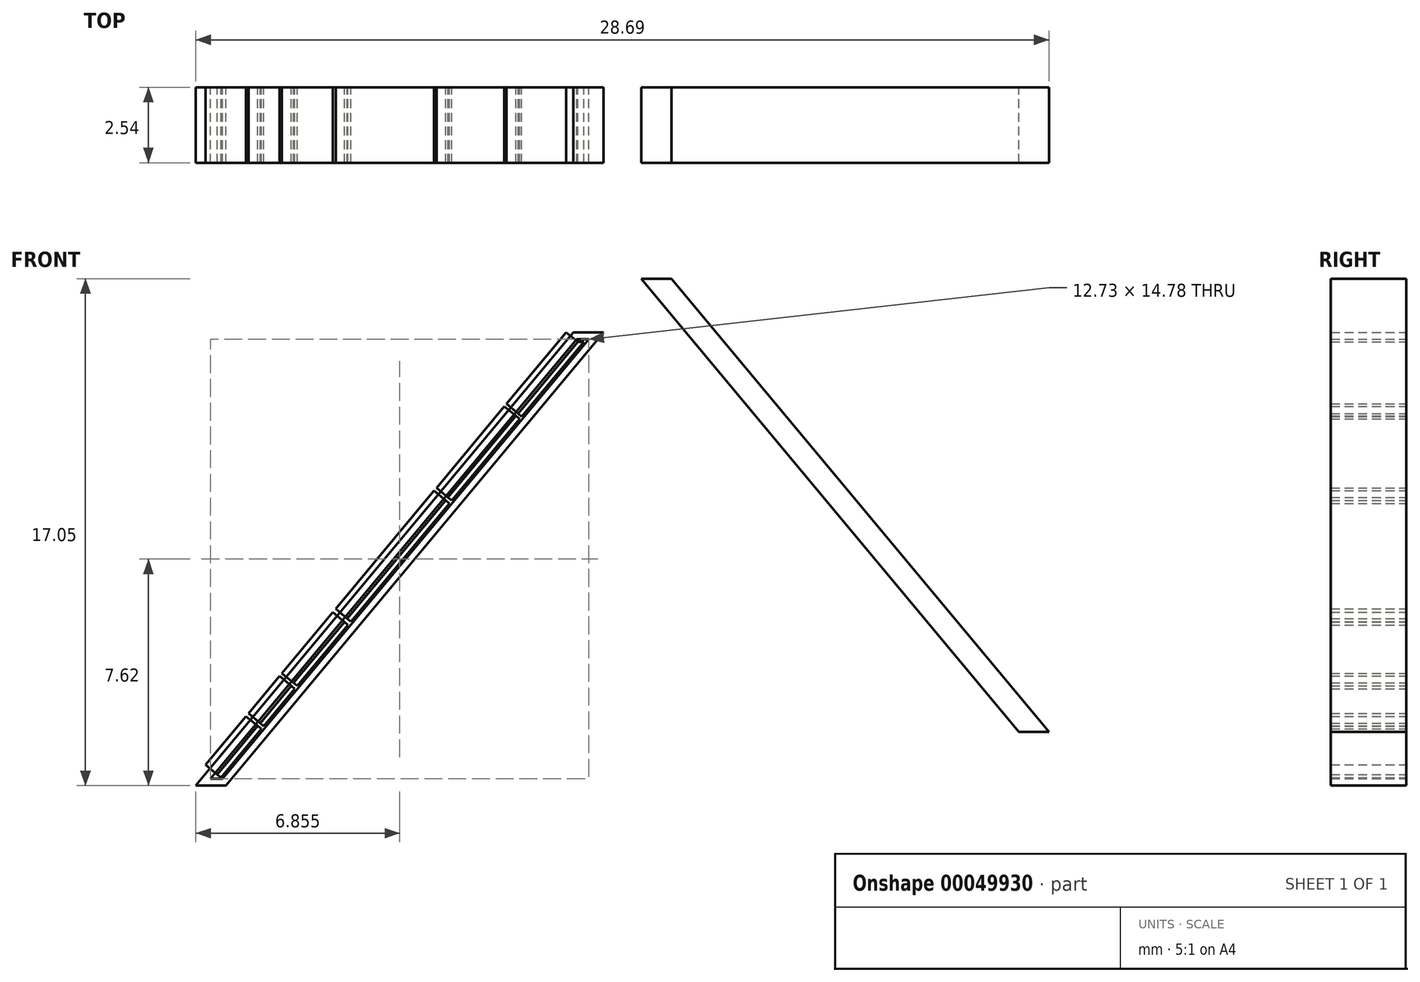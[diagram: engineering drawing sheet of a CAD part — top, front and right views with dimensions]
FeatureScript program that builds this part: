
annotation { "Feature Type Name" : "Feature", "Feature Type Description" : "" }
export const myFeature = defineFeature(function(context is Context, id is Id, definition is map)
    precondition{}
    {
        {
            var Q0;
            Q0=qCreatedBy(makeId("Front.planeOp"),FACE);
            var sketch = newSketch(context, id + "F0", { "sketchPlane" : qUnion([Q0])});
            skLineSegment(sketch, "E0", {"start": v(36.54, 21.91) * mm, "end": v(23.84, 6.67) * mm});
            skLineSegment(sketch, "E1", {"start": v(23.84, 6.67) * mm, "end": v(24.85, 6.67) * mm, "construction": true});
            skLineSegment(sketch, "E2", {"start": v(36.54, 21.91) * mm, "end": v(37.55, 21.91) * mm});
            skLineSegment(sketch, "E3", {"start": v(37.55, 21.91) * mm, "end": v(24.85, 6.67) * mm});
            skLineSegment(sketch, "E4", {"start": v(23.84, 6.67) * mm, "end": v(24.14, 6.67) * mm});
            skLineSegment(sketch, "E5", {"start": v(24.85, 6.67) * mm, "end": v(24.55, 6.67) * mm});
            skLineSegment(sketch, "E6", {"start": v(24.14, 6.67) * mm, "end": v(36.84, 21.91) * mm});
            skLineSegment(sketch, "E7", {"start": v(24.55, 6.67) * mm, "end": v(37.25, 21.91) * mm});
            skPoint(sketch, "E7.endSnap0", {"position": v(37.04, 21.91) * mm});
            skLineSegment(sketch, "E8", {"start": v(36.84, 21.91) * mm, "end": v(36.84, 21.68) * mm});
            skLineSegment(sketch, "E9", {"start": v(36.84, 21.68) * mm, "end": v(36.65, 21.68) * mm});
            skLineSegment(sketch, "E10", {"start": v(36.65, 21.68) * mm, "end": v(37.06, 21.68) * mm});
            skLineSegment(sketch, "E11", {"start": v(24.34, 6.67) * mm, "end": v(24.34, 6.9) * mm});
            skLineSegment(sketch, "E12", {"start": v(24.34, 6.9) * mm, "end": v(24.74, 6.9) * mm});
            skLineSegment(sketch, "E13", {"start": v(24.74, 6.9) * mm, "end": v(24.33, 6.9) * mm});
            skLineSegment(sketch, "E14", {"start": v(24.14, 6.67) * mm, "end": v(24.55, 6.67) * mm});
            skLineSegment(sketch, "E15", {"start": v(24.56, 6.9) * mm, "end": v(24.56, 7.04) * mm});
            skLineSegment(sketch, "E16", {"start": v(24.56, 7.04) * mm, "end": v(24.45, 7.04) * mm});
            skLineSegment(sketch, "E17", {"start": v(24.56, 7.04) * mm, "end": v(24.81, 7.35) * mm});
            skLineSegment(sketch, "E18", {"start": v(24.81, 7.35) * mm, "end": v(24.93, 7.25) * mm});
            skLineSegment(sketch, "E19", {"start": v(24.56, 7.04) * mm, "end": v(24.68, 6.94) * mm});
            skLineSegment(sketch, "E20", {"start": v(24.93, 7.25) * mm, "end": v(24.68, 6.94) * mm});
            skLineSegment(sketch, "E21", {"start": v(24.81, 7.35) * mm, "end": v(24.87, 7.42) * mm});
            skPoint(sketch, "E21.endSnap0", {"position": v(24.87, 7.3) * mm});
            skLineSegment(sketch, "E22", {"start": v(24.87, 7.42) * mm, "end": v(24.99, 7.32) * mm});
            skLineSegment(sketch, "E23", {"start": v(24.99, 7.32) * mm, "end": v(25.32, 7.72) * mm});
            skLineSegment(sketch, "E24", {"start": v(24.87, 7.42) * mm, "end": v(25.2, 7.82) * mm});
            skLineSegment(sketch, "E25", {"start": v(25.2, 7.82) * mm, "end": v(25.32, 7.72) * mm});
            skLineSegment(sketch, "E26", {"start": v(25.2, 7.82) * mm, "end": v(25.24, 7.86) * mm});
            skLineSegment(sketch, "E27", {"start": v(25.24, 7.86) * mm, "end": v(25.35, 7.77) * mm});
            skLineSegment(sketch, "E28", {"start": v(25.35, 7.77) * mm, "end": v(25.51, 7.96) * mm});
            skLineSegment(sketch, "E29", {"start": v(25.24, 7.86) * mm, "end": v(25.4, 8.05) * mm});
            skLineSegment(sketch, "E30", {"start": v(25.4, 8.05) * mm, "end": v(25.51, 7.96) * mm});
            skLineSegment(sketch, "E31", {"start": v(25.4, 8.05) * mm, "end": v(25.44, 8.1) * mm});
            skLineSegment(sketch, "E32", {"start": v(25.44, 8.1) * mm, "end": v(25.54, 8) * mm});
            skLineSegment(sketch, "E33", {"start": v(25.54, 8) * mm, "end": v(25.75, 8.26) * mm});
            skLineSegment(sketch, "E34", {"start": v(25.44, 8.1) * mm, "end": v(25.65, 8.35) * mm});
            skLineSegment(sketch, "E35", {"start": v(25.65, 8.35) * mm, "end": v(25.75, 8.26) * mm});
            skLineSegment(sketch, "E36", {"start": v(25.65, 8.35) * mm, "end": v(25.68, 8.4) * mm});
            skLineSegment(sketch, "E37", {"start": v(25.68, 8.4) * mm, "end": v(25.78, 8.31) * mm});
            skLineSegment(sketch, "E38", {"start": v(25.78, 8.31) * mm, "end": v(25.93, 8.5) * mm});
            skLineSegment(sketch, "E39", {"start": v(25.68, 8.4) * mm, "end": v(25.83, 8.58) * mm});
            skLineSegment(sketch, "E40", {"start": v(25.83, 8.58) * mm, "end": v(25.93, 8.5) * mm});
            skLineSegment(sketch, "E41", {"start": v(24.68, 6.94) * mm, "end": v(26.04, 8.58) * mm});
            skLineSegment(sketch, "E42", {"start": v(26.04, 8.58) * mm, "end": v(25.92, 8.68) * mm});
            skLineSegment(sketch, "E43", {"start": v(25.83, 8.58) * mm, "end": v(25.92, 8.68) * mm});
            skLineSegment(sketch, "E44", {"start": v(26, 8.78) * mm, "end": v(26.12, 8.68) * mm});
            skLineSegment(sketch, "E45", {"start": v(26.12, 8.68) * mm, "end": v(27.16, 9.93) * mm});
            skLineSegment(sketch, "E46", {"start": v(26, 8.78) * mm, "end": v(27.04, 10.03) * mm});
            skLineSegment(sketch, "E47", {"start": v(27.04, 10.03) * mm, "end": v(27.16, 9.93) * mm});
            skLineSegment(sketch, "E48", {"start": v(27.12, 10.12) * mm, "end": v(27.25, 10.02) * mm});
            skLineSegment(sketch, "E49", {"start": v(27.25, 10.02) * mm, "end": v(28.96, 12.08) * mm});
            skLineSegment(sketch, "E50", {"start": v(27.12, 10.12) * mm, "end": v(28.84, 12.18) * mm});
            skLineSegment(sketch, "E51", {"start": v(28.84, 12.18) * mm, "end": v(28.96, 12.08) * mm});
            skLineSegment(sketch, "E52", {"start": v(28.93, 12.29) * mm, "end": v(29.05, 12.19) * mm});
            skLineSegment(sketch, "E53", {"start": v(29.05, 12.19) * mm, "end": v(32.36, 16.17) * mm});
            skLineSegment(sketch, "E54", {"start": v(28.93, 12.29) * mm, "end": v(32.24, 16.27) * mm});
            skLineSegment(sketch, "E55", {"start": v(32.24, 16.27) * mm, "end": v(32.36, 16.17) * mm});
            skLineSegment(sketch, "E56", {"start": v(32.24, 16.27) * mm, "end": v(32.32, 16.36) * mm});
            skLineSegment(sketch, "E57", {"start": v(32.36, 16.17) * mm, "end": v(34.73, 19) * mm});
            skLineSegment(sketch, "E58", {"start": v(34.73, 19) * mm, "end": v(34.57, 19.13) * mm});
            skLineSegment(sketch, "E59", {"start": v(32.32, 16.36) * mm, "end": v(32.44, 16.26) * mm});
            skLineSegment(sketch, "E60", {"start": v(32.32, 16.36) * mm, "end": v(34.6, 19.1) * mm});
            skLineSegment(sketch, "E61", {"start": v(34.68, 19.19) * mm, "end": v(34.8, 19.09) * mm});
            skLineSegment(sketch, "E62", {"start": v(34.68, 19.19) * mm, "end": v(36.68, 21.6) * mm});
            skLineSegment(sketch, "E63", {"start": v(34.8, 19.09) * mm, "end": v(36.89, 21.6) * mm});
            skLineSegment(sketch, "E64", {"start": v(36.68, 21.6) * mm, "end": v(36.89, 21.6) * mm});
            skLineSegment(sketch, "E65", {"start": v(39.83, 23.72) * mm, "end": v(52.53, 8.48) * mm});
            skLineSegment(sketch, "E66", {"start": v(52.53, 8.48) * mm, "end": v(51.52, 8.48) * mm});
            skLineSegment(sketch, "E67", {"start": v(39.83, 23.72) * mm, "end": v(38.82, 23.72) * mm});
            skLineSegment(sketch, "E68", {"start": v(38.82, 23.72) * mm, "end": v(51.52, 8.48) * mm});
            skSolve(sketch);
        }
        {
            var Q0;
            Q0 = qSketchRegion(id + "F0", true);
            var Q1;
            Q1=makeQuery(id+"F0.imprint","IMPRINT",FACE,{"disambiguationData":[TD([[makeQuery(id+"F0.imprint","IMPRINT",EDGE,{"derivedFrom":sQuery(id+"F0.wireOp",EDGE,"cbd0a447-a393-4120-82ce-9e7111b09477")}),-1.0]])]});
            var Q2;
            Q2=makeQuery(id+"F0.imprint","IMPRINT",FACE,{"disambiguationData":[TD([[makeQuery(id+"F0.imprint","IMPRINT",EDGE,{"derivedFrom":sQuery(id+"F0.wireOp",EDGE,"cbd0a447-a393-4120-82ce-9e7111b09477")}),1.0]])]});
            var Q3;
            Q3=makeQuery(id+"F0.imprint","IMPRINT",FACE,{"disambiguationData":[TD([[makeQuery(id+"F0.imprint","IMPRINT",EDGE,{"derivedFrom":sQuery(id+"F0.wireOp",EDGE,"E32")}),1.0]])]});
            var Q4;
            {var subQ0=sQuery(id+"F0.wireOp",EDGE,"E18");Q4=makeQuery(id+"F0.imprint","IMPRINT",FACE,{"disambiguationData":[TD([[makeQuery(id+"F0.imprint","IMPRINT",EDGE,{"derivedFrom":subQ0}),1.0]])]});}
            var Q5;
            Q5=makeQuery(id+"F0.imprint","IMPRINT",FACE,{"disambiguationData":[TD([[makeQuery(id+"F0.imprint","IMPRINT",EDGE,{"derivedFrom":sQuery(id+"F0.wireOp",EDGE,"E37")}),1.0]])]});
            var Q6;
            Q6=makeQuery(id+"F0.imprint","IMPRINT",FACE,{"disambiguationData":[TD([[makeQuery(id+"F0.imprint","IMPRINT",EDGE,{"derivedFrom":sQuery(id+"F0.wireOp",EDGE,"E27")}),1.0]])]});
            var Q7;
            Q7=makeQuery(id+"F0.imprint","IMPRINT",FACE,{"disambiguationData":[TD([[makeQuery(id+"F0.imprint","IMPRINT",EDGE,{"derivedFrom":sQuery(id+"F0.wireOp",EDGE,"E22")}),1.0]])]});
            var Q8;
            Q8=makeQuery(id+"F0.imprint","IMPRINT",FACE,{"disambiguationData":[TD([[makeQuery(id+"F0.imprint","IMPRINT",EDGE,{"derivedFrom":sQuery(id+"F0.wireOp",EDGE,"E17")}),-1.0]])]});
            var Q9;
            Q9=makeQuery(id+"F0.imprint","IMPRINT",FACE,{"disambiguationData":[TD([[makeQuery(id+"F0.imprint","IMPRINT",EDGE,{"derivedFrom":sQuery(id+"F0.wireOp",EDGE,"E44")}),1.0]])]});
            var Q10;
            Q10=makeQuery(id+"F0.imprint","IMPRINT",FACE,{"disambiguationData":[TD([[makeQuery(id+"F0.imprint","IMPRINT",EDGE,{"derivedFrom":sQuery(id+"F0.wireOp",EDGE,"E48")}),1.0]])]});
            var Q11;
            Q11=makeQuery(id+"F0.imprint","IMPRINT",FACE,{"disambiguationData":[TD([[makeQuery(id+"F0.imprint","IMPRINT",EDGE,{"derivedFrom":sQuery(id+"F0.wireOp",EDGE,"E52")}),1.0]])]});
            var Q12;
            {var subQ3=sQuery(id+"F0.wireOp",EDGE,"E59");Q12=makeQuery(id+"F0.imprint","IMPRINT",FACE,{"disambiguationData":[TD([[makeQuery(id+"F0.imprint","IMPRINT",EDGE,{"derivedFrom":subQ3}),1.0]])]});}
            var Q13;
            Q13=makeQuery(id+"F0.imprint","IMPRINT",FACE,{"disambiguationData":[TD([[makeQuery(id+"F0.imprint","IMPRINT",EDGE,{"derivedFrom":sQuery(id+"F0.wireOp",EDGE,"E61")}),1.0]])]});
            extrude(context, id + "F1", {"entities" : qUnion([Q0, Q1, Q2, Q3, Q4, Q5, Q6, Q7, Q8, Q9, Q10, Q11, Q12, Q13]), "depth" : 2.54 * mm});
        }
        {
            var Q0;
            Q0=makeQuery(id+"F1.opExtrude","SWEPT_FACE",FACE,{"disambiguationData":[OSD([sQuery(id+"F0.wireOp",EDGE,"E17"),sQuery(id+"F0.wireOp",EDGE,"E21"),sQuery(id+"F0.wireOp",EDGE,"E24"),sQuery(id+"F0.wireOp",EDGE,"E26"),sQuery(id+"F0.wireOp",EDGE,"E29"),sQuery(id+"F0.wireOp",EDGE,"E31"),sQuery(id+"F0.wireOp",EDGE,"E34"),sQuery(id+"F0.wireOp",EDGE,"E36"),sQuery(id+"F0.wireOp",EDGE,"E39"),sQuery(id+"F0.wireOp",EDGE,"E43")])]});
            extrude(context, id + "F2", {"entities" : qUnion([Q0]), "depth" : 0.5 * mm});
        }
        {
            var Q0;
            Q0=makeQuery(id+"F1.opExtrude","SWEPT_FACE",FACE,{"disambiguationData":[OSD([sQuery(id+"F0.wireOp",EDGE,"E46")])]});
            extrude(context, id + "F3", {"entities" : qUnion([Q0]), "depth" : 0.5 * mm});
        }
        {
            var Q0;
            Q0=makeQuery(id+"F1.opExtrude","SWEPT_FACE",FACE,{"disambiguationData":[OSD([sQuery(id+"F0.wireOp",EDGE,"E50")])]});
            extrude(context, id + "F4", {"entities" : qUnion([Q0]), "depth" : 0.5 * mm});
        }
        {
            var Q0;
            Q0=makeQuery(id+"F1.opExtrude","SWEPT_FACE",FACE,{"disambiguationData":[OSD([sQuery(id+"F0.wireOp",EDGE,"E54")])]});
            extrude(context, id + "F5", {"entities" : qUnion([Q0]), "depth" : 0.5 * mm});
        }
        {
            var Q0;
            Q0=makeQuery(id+"F1.opExtrude","SWEPT_FACE",FACE,{"disambiguationData":[OSD([sQuery(id+"F0.wireOp",EDGE,"E60")])]});
            extrude(context, id + "F6", {"entities" : qUnion([Q0]), "depth" : 0.5 * mm});
        }
        {
            var Q0;
            Q0=makeQuery(id+"F1.opExtrude","SWEPT_FACE",FACE,{"disambiguationData":[OSD([sQuery(id+"F0.wireOp",EDGE,"E62")])]});
            extrude(context, id + "F7", {"entities" : qUnion([Q0]), "depth" : 0.5 * mm});
        }
    });
